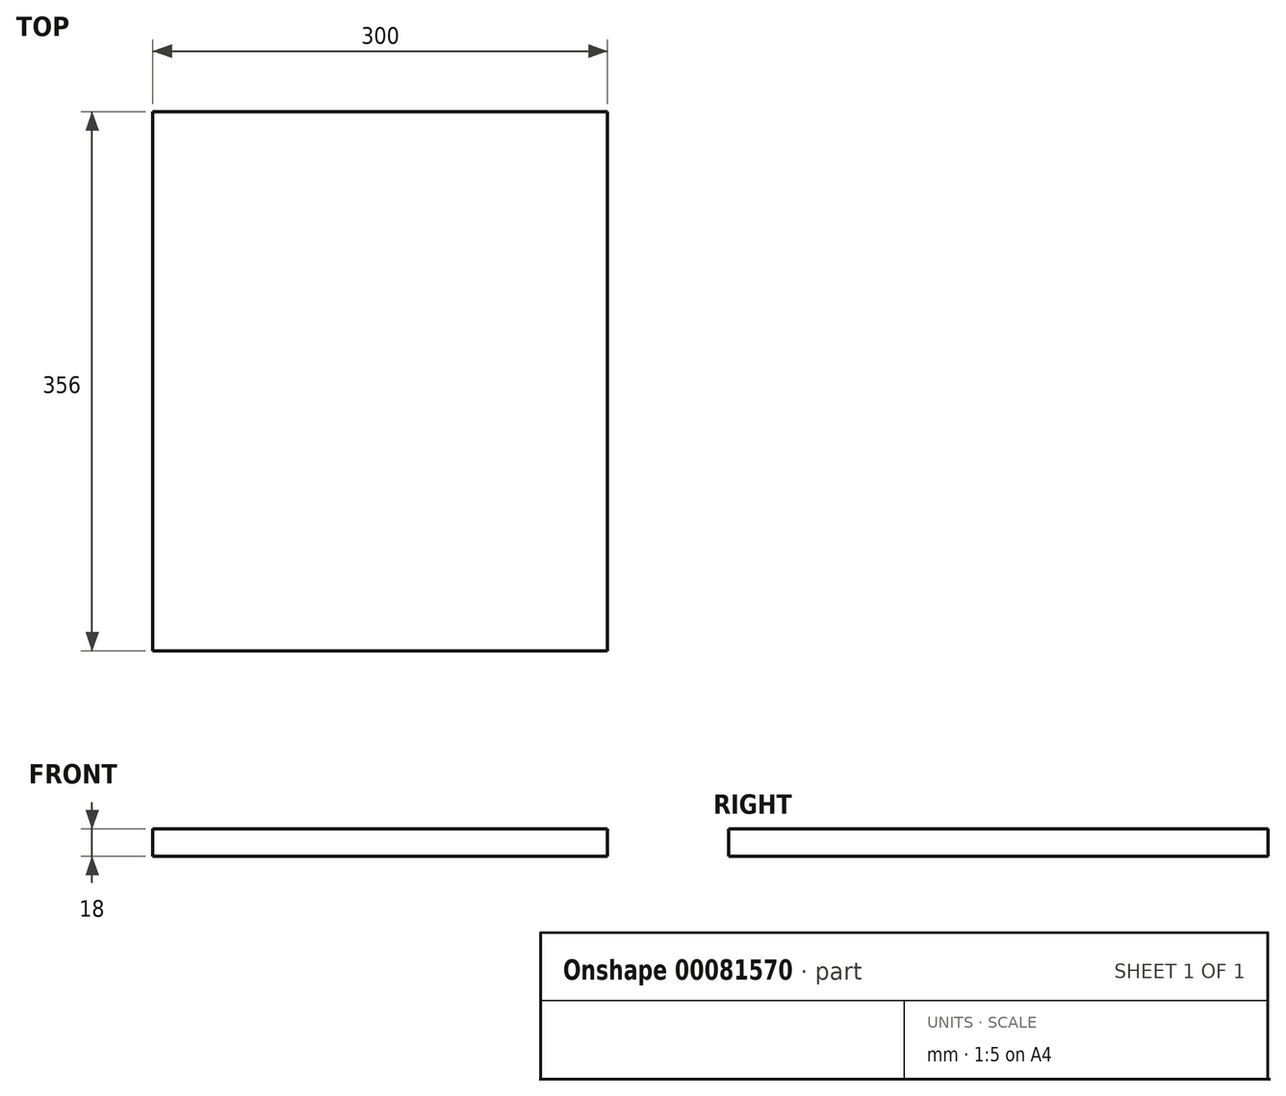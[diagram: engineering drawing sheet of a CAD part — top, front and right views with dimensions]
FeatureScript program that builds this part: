
annotation { "Feature Type Name" : "Feature", "Feature Type Description" : "" }
export const myFeature = defineFeature(function(context is Context, id is Id, definition is map)
    precondition{}
    {
        {
            var Q0;
            Q0=qCreatedBy(makeId("Top.planeOp"),FACE);
            var sketch = newSketch(context, id + "F0", { "sketchPlane" : qUnion([Q0])});
            skLineSegment(sketch, "E0.bottom", {"start": v(0, 0) * mm, "end": v(300, 0) * mm});
            skLineSegment(sketch, "E0.top", {"start": v(0, 356) * mm, "end": v(300, 356) * mm});
            skLineSegment(sketch, "E0.left", {"start": v(0, 0) * mm, "end": v(0, 356) * mm});
            skLineSegment(sketch, "E0.right", {"start": v(300, 0) * mm, "end": v(300, 356) * mm});
            skSolve(sketch);
        }
        {
            var Q0;
            Q0 = qSketchRegion(id + "F0", true);
            extrude(context, id + "F1", {"entities" : qUnion([Q0]), "depth" : 18 * mm});
        }
    });
